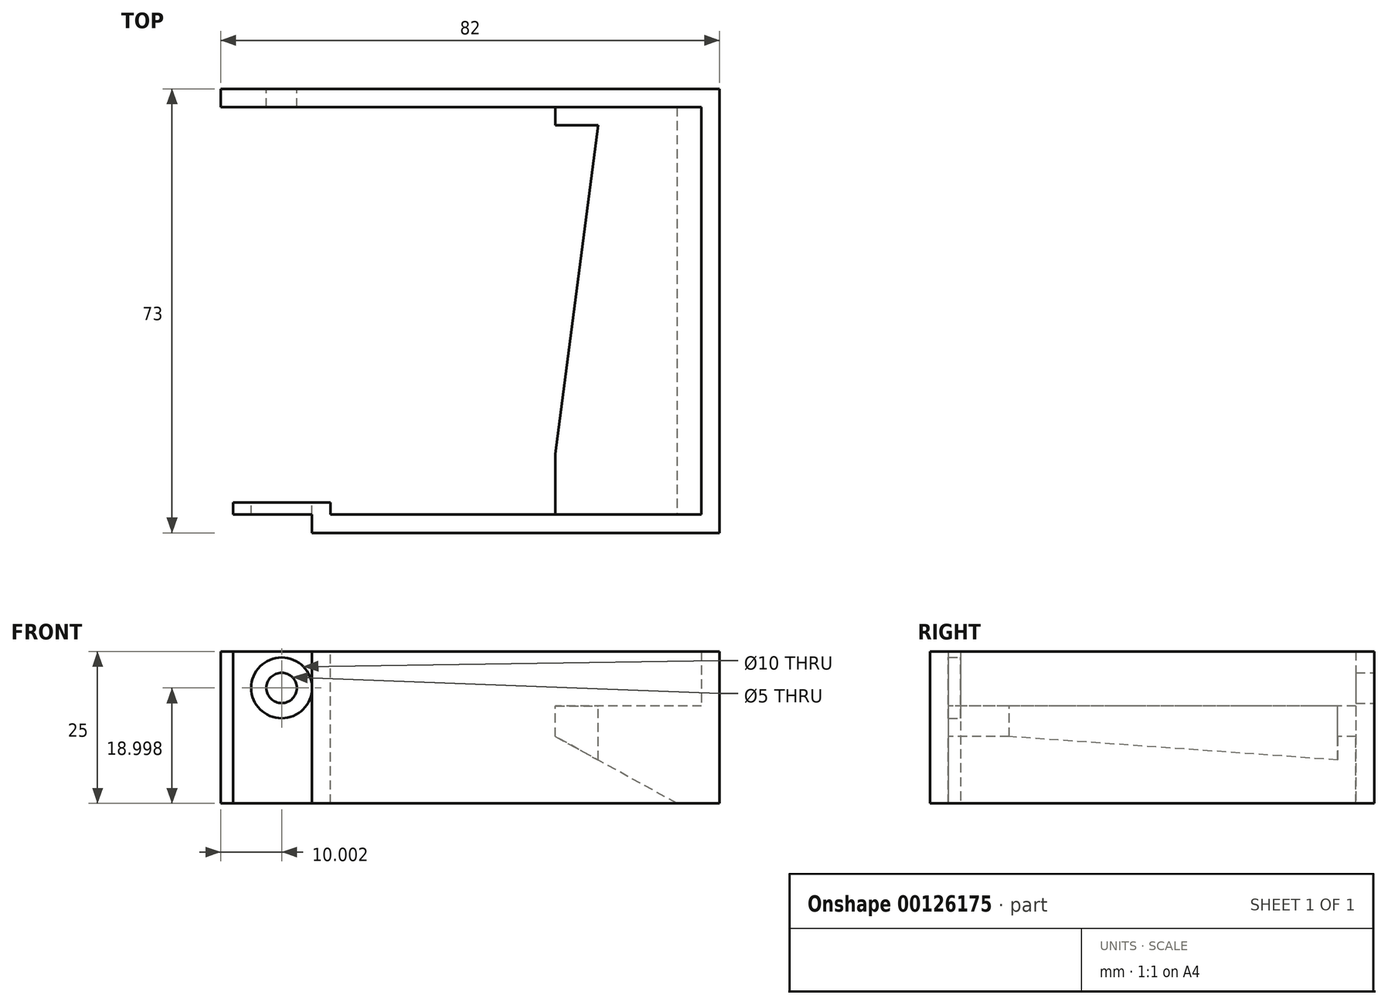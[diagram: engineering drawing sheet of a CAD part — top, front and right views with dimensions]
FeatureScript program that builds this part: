
annotation { "Feature Type Name" : "Feature", "Feature Type Description" : "" }
export const myFeature = defineFeature(function(context is Context, id is Id, definition is map)
    precondition{}
    {
        {
            var Q0;
            Q0=qCreatedBy(makeId("Front.planeOp"),FACE);
            var sketch = newSketch(context, id + "F0", { "sketchPlane" : qUnion([Q0])});
            skLineSegment(sketch, "E0.bottom", {"start": v(-28.48, 9.04) * mm, "end": v(-12.48, 9.04) * mm});
            skLineSegment(sketch, "E0.top", {"start": v(-28.48, -15.96) * mm, "end": v(-12.48, -15.96) * mm});
            skLineSegment(sketch, "E0.left", {"start": v(-28.48, 9.04) * mm, "end": v(-28.48, -15.96) * mm});
            skLineSegment(sketch, "E0.right", {"start": v(-12.48, 9.04) * mm, "end": v(-12.48, -15.96) * mm});
            skLineSegment(sketch, "E1", {"start": v(-20.48, -15.96) * mm, "end": v(-20.48, 3.04) * mm, "construction": true});
            skCircle(sketch, "E2", {"center": v(-20.48, 3.04) * mm, "radius": 5 * mm});
            skLineSegment(sketch, "E3", {"start": v(-28.48, 3.04) * mm, "end": v(-20.48, 3.04) * mm, "construction": true});
            skSolve(sketch);
        }
        {
            var Q0;
            Q0 = qSketchRegion(id + "F0", true);
            extrude(context, id + "F1", {"entities" : qUnion([Q0]), "depth" : 2 * mm});
        }
        {
            var Q0;
            Q0=makeQuery(id+"F1.opExtrude","CAP_FACE",FACE,{"disambiguationData":[OSD([sQuery(id+"F0.wireOp",EDGE,"E0.bottom"),sQuery(id+"F0.wireOp",EDGE,"E0.top"),sQuery(id+"F0.wireOp",EDGE,"E0.left"),sQuery(id+"F0.wireOp",EDGE,"E0.right"),sQuery(id+"F0.wireOp",EDGE,"E2")])],"isStart":false});
            var sketch = newSketch(context, id + "F2", { "sketchPlane" : qUnion([Q0])});
            skLineSegment(sketch, "E4.bottom", {"start": v(-12.48, 9.04) * mm, "end": v(-15.48, 9.04) * mm});
            skLineSegment(sketch, "E4.top", {"start": v(-12.48, -15.96) * mm, "end": v(-15.48, -15.96) * mm});
            skLineSegment(sketch, "E4.left", {"start": v(-12.48, 9.04) * mm, "end": v(-12.48, -15.96) * mm});
            skLineSegment(sketch, "E4.right", {"start": v(-15.48, 9.04) * mm, "end": v(-15.48, -15.96) * mm});
            skSolve(sketch);
        }
        {
            var Q0;
            Q0 = qSketchRegion(id + "F2", true);
            extrude(context, id + "F3", {"entities" : qUnion([Q0]), "operationType" : NewBodyOperationType.ADD, "depth" : 3 * mm});
        }
        {
            var Q0;
            Q0=makeQuery(id+"F3.boolean.opBoolean","MERGE",FACE,{"derivedFrom":[makeQuery(id+"F1.opExtrude","SWEPT_FACE",FACE,{"disambiguationData":[OSD([sQuery(id+"F0.wireOp",EDGE,"E0.right")])]}),makeQuery(id+"F3.opExtrude","SWEPT_FACE",FACE,{"disambiguationData":[OSD([sQuery(id+"F2.wireOp",EDGE,"E4.left")])]})]});
            var sketch = newSketch(context, id + "F4", { "sketchPlane" : qUnion([Q0])});
            skLineSegment(sketch, "E5.bottom", {"start": v(-5, -15.96) * mm, "end": v(-2, -15.96) * mm});
            skLineSegment(sketch, "E5.top", {"start": v(-5, 9.04) * mm, "end": v(-2, 9.04) * mm});
            skLineSegment(sketch, "E5.left", {"start": v(-5, -15.96) * mm, "end": v(-5, 9.04) * mm});
            skLineSegment(sketch, "E5.right", {"start": v(-2, -15.96) * mm, "end": v(-2, 9.04) * mm});
            skSolve(sketch);
        }
        {
            var Q0;
            Q0 = qSketchRegion(id + "F4", true);
            extrude(context, id + "F5", {"entities" : qUnion([Q0]), "operationType" : NewBodyOperationType.ADD, "depth" : 65 * mm});
        }
        {
            var Q0;
            Q0=makeQuery(id+"F5.opExtrude","SWEPT_FACE",FACE,{"disambiguationData":[OSD([sQuery(id+"F4.wireOp",EDGE,"E5.right")])]});
            var sketch = newSketch(context, id + "F6", { "sketchPlane" : qUnion([Q0])});
            skLineSegment(sketch, "E6.bottom", {"start": v(-52.52, 9.04) * mm, "end": v(-49.52, 9.04) * mm});
            skLineSegment(sketch, "E6.top", {"start": v(-52.52, -15.96) * mm, "end": v(-49.52, -15.96) * mm});
            skLineSegment(sketch, "E6.left", {"start": v(-52.52, 9.04) * mm, "end": v(-52.52, -15.96) * mm});
            skLineSegment(sketch, "E6.right", {"start": v(-49.52, 9.04) * mm, "end": v(-49.52, -15.96) * mm});
            skSolve(sketch);
        }
        {
            var Q0;
            Q0 = qSketchRegion(id + "F6", true);
            extrude(context, id + "F7", {"entities" : qUnion([Q0]), "operationType" : NewBodyOperationType.ADD, "depth" : 70 * mm});
        }
        {
            var Q0;
            Q0=makeQuery(id+"F1.opExtrude","CAP_FACE",FACE,{"disambiguationData":[OSD([sQuery(id+"F0.wireOp",EDGE,"E0.bottom"),sQuery(id+"F0.wireOp",EDGE,"E0.top"),sQuery(id+"F0.wireOp",EDGE,"E0.left"),sQuery(id+"F0.wireOp",EDGE,"E0.right"),sQuery(id+"F0.wireOp",EDGE,"E2")])],"isStart":true});
            var sketch = newSketch(context, id + "F8", { "sketchPlane" : qUnion([Q0])});
            skCircle(sketch, "E7", {"center": v(20.48, 3.04) * mm, "radius": 15 * mm, "construction": true});
            skSolve(sketch);
        }
        {
            var Q0;
            Q0=makeQuery(id+"F5.opExtrude","SWEPT_FACE",FACE,{"disambiguationData":[OSD([sQuery(id+"F4.wireOp",EDGE,"E5.right")])]});
            var sketch = newSketch(context, id + "F9", { "sketchPlane" : qUnion([Q0])});
            skLineSegment(sketch, "E8", {"start": v(-49.52, -15.96) * mm, "end": v(-49.52, 0.04) * mm});
            skLineSegment(sketch, "E9", {"start": v(-49.52, 0.04) * mm, "end": v(-24.52, 0.04) * mm});
            skLineSegment(sketch, "E10", {"start": v(20.48, 3.04) * mm, "end": v(-53.47, 3.04) * mm, "construction": true});
            skLineSegment(sketch, "E11", {"start": v(-49.52, -15.96) * mm, "end": v(-44.52, -15.96) * mm});
            skLineSegment(sketch, "E12", {"start": v(-44.52, -15.96) * mm, "end": v(-49.52, -15.96) * mm});
            skLineSegment(sketch, "E13", {"start": v(-24.52, 0.04) * mm, "end": v(-24.52, -4.96) * mm});
            skLineSegment(sketch, "E14", {"start": v(-44.52, -15.96) * mm, "end": v(-24.52, -4.96) * mm});
            skSolve(sketch);
        }
        {
            var Q0;
            Q0 = qSketchRegion(id + "F9", true);
            extrude(context, id + "F10", {"entities" : qUnion([Q0]), "operationType" : NewBodyOperationType.ADD, "depth" : 67 * mm});
        }
        {
            var Q0;
            Q0=makeQuery(id+"F7.opExtrude","SWEPT_FACE",FACE,{"disambiguationData":[OSD([sQuery(id+"F6.wireOp",EDGE,"E6.right")])]});
            var sketch = newSketch(context, id + "F11", { "sketchPlane" : qUnion([Q0])});
            skLineSegment(sketch, "E15.bottom", {"start": v(-68, 9.04) * mm, "end": v(-65, 9.04) * mm});
            skLineSegment(sketch, "E15.top", {"start": v(-68, -15.96) * mm, "end": v(-65, -15.96) * mm});
            skLineSegment(sketch, "E15.left", {"start": v(-68, 9.04) * mm, "end": v(-68, -15.96) * mm});
            skLineSegment(sketch, "E15.right", {"start": v(-65, 9.04) * mm, "end": v(-65, -15.96) * mm});
            skSolve(sketch);
        }
        {
            var Q0;
            Q0 = qSketchRegion(id + "F11", true);
            extrude(context, id + "F12", {"entities" : qUnion([Q0]), "operationType" : NewBodyOperationType.ADD, "depth" : 80 * mm});
        }
        {
            var Q0;
            Q0=makeQuery(id+"F12.boolean.opBoolean","MERGE",FACE,{"derivedFrom":[makeQuery(id+"F7.opExtrude","CAP_FACE",FACE,{"disambiguationData":[OSD([sQuery(id+"F6.wireOp",EDGE,"E6.bottom"),sQuery(id+"F6.wireOp",EDGE,"E6.top"),sQuery(id+"F6.wireOp",EDGE,"E6.left"),sQuery(id+"F6.wireOp",EDGE,"E6.right")])],"isStart":false}),makeQuery(id+"F12.opExtrude","SWEPT_FACE",FACE,{"disambiguationData":[OSD([sQuery(id+"F11.wireOp",EDGE,"E15.left")])]})]});
            var sketch = newSketch(context, id + "F13", { "sketchPlane" : qUnion([Q0])});
            skCircle(sketch, "E16", {"center": v(20.48, 3.04) * mm, "radius": 2.5 * mm});
            skSolve(sketch);
        }
        {
            var Q0;
            Q0 = qSketchRegion(id + "F13", true);
            extrude(context, id + "F14", {"entities" : qUnion([Q0]), "operationType" : NewBodyOperationType.REMOVE, "oppositeDirection" : true, "depth" : 3 * mm});
        }
        {
            var Q0;
            Q0=makeQuery(id+"F10.opExtrude","SWEPT_FACE",FACE,{"disambiguationData":[OSD([sQuery(id+"F9.wireOp",EDGE,"E9")])]});
            var sketch = newSketch(context, id + "F15", { "sketchPlane" : qUnion([Q0])});
            skLineSegment(sketch, "E17", {"start": v(24.52, 65) * mm, "end": v(24.52, 62) * mm, "construction": true});
            skLineSegment(sketch, "E18", {"start": v(24.52, 62) * mm, "end": v(24.52, 8) * mm});
            skLineSegment(sketch, "E19", {"start": v(24.52, 62) * mm, "end": v(31.52, 62) * mm});
            skLineSegment(sketch, "E20", {"start": v(31.52, 62) * mm, "end": v(24.52, 8) * mm});
            skLineSegment(sketch, "E21", {"start": v(31.52, 62) * mm, "end": v(49.52, 62) * mm, "construction": true});
            skSolve(sketch);
        }
        {
            var Q0;
            Q0 = qSketchRegion(id + "F15", true);
            extrude(context, id + "F16", {"entities" : qUnion([Q0]), "operationType" : NewBodyOperationType.REMOVE, "endBound" : BoundingType.THROUGH_ALL, "oppositeDirection" : true, "depth" : 25 * mm});
        }
        {
            var Q0;
            Q0=makeQuery(id+"F10.opExtrude","SWEPT_FACE",FACE,{"disambiguationData":[OSD([sQuery(id+"F9.wireOp",EDGE,"E9")])]});
            var sketch = newSketch(context, id + "F17", { "sketchPlane" : qUnion([Q0])});
            skLineSegment(sketch, "E22.bottom", {"start": v(49.52, 65) * mm, "end": v(48.52, 65) * mm});
            skLineSegment(sketch, "E22.top", {"start": v(49.52, -2) * mm, "end": v(48.52, -2) * mm});
            skLineSegment(sketch, "E22.left", {"start": v(49.52, 65) * mm, "end": v(49.52, -2) * mm});
            skLineSegment(sketch, "E22.right", {"start": v(48.52, 65) * mm, "end": v(48.52, -2) * mm});
            skSolve(sketch);
        }
        {
            var Q0;
            Q0 = qSketchRegion(id + "F17", true);
            var Q1;
            {var subQ1=sQuery(id+"F0.wireOp",EDGE,"E0.left");var subQ3=sQuery(id+"F2.wireOp",EDGE,"E4.bottom");var subQ7=sQuery(id+"F0.wireOp",EDGE,"E0.bottom");var subQ10=sQuery(id+"F4.wireOp",EDGE,"E5.top");var subQ13=sQuery(id+"F6.wireOp",EDGE,"E6.bottom");Q1=makeQuery(id+"F14.boolean.opBoolean","SPLIT",FACE,{"disambiguationData":[TD([makeQuery(id+"F1.opExtrude","SWEPT_FACE",FACE,{"disambiguationData":[OSD([subQ1])]})])],"derivedFrom":makeQuery(id+"F12.boolean.opBoolean","MERGE",FACE,{"derivedFrom":[makeQuery(id+"F7.boolean.opBoolean","MERGE",FACE,{"derivedFrom":[makeQuery(id+"F5.boolean.opBoolean","MERGE",FACE,{"derivedFrom":[makeQuery(id+"F3.boolean.opBoolean","MERGE",FACE,{"derivedFrom":[makeQuery(id+"F1.opExtrude","SWEPT_FACE",FACE,{"disambiguationData":[OSD([subQ7])]}),makeQuery(id+"F3.opExtrude","SWEPT_FACE",FACE,{"disambiguationData":[OSD([subQ3])]})]}),makeQuery(id+"F5.opExtrude","SWEPT_FACE",FACE,{"disambiguationData":[OSD([subQ10])]})]}),makeQuery(id+"F7.opExtrude","SWEPT_FACE",FACE,{"disambiguationData":[OSD([subQ13])]})]}),makeQuery(id+"F12.opExtrude","SWEPT_FACE",FACE,{"disambiguationData":[OSD([sQuery(id+"F11.wireOp",EDGE,"E15.bottom")])]})]})});}
            extrude(context, id + "F18", {"entities" : qUnion([Q0]), "operationType" : NewBodyOperationType.ADD, "endBound" : BoundingType.UP_TO_SURFACE, "endBoundEntityFace" : qUnion([Q1]), "depth" : 25 * mm});
        }
        {
            var Q0;
            {var subQ1=sQuery(id+"F0.wireOp",EDGE,"E0.left");var subQ3=sQuery(id+"F2.wireOp",EDGE,"E4.bottom");var subQ7=sQuery(id+"F0.wireOp",EDGE,"E0.bottom");var subQ10=sQuery(id+"F4.wireOp",EDGE,"E5.top");var subQ13=sQuery(id+"F6.wireOp",EDGE,"E6.bottom");Q0=makeQuery(id+"F18.boolean.opBoolean","MERGE",FACE,{"derivedFrom":[makeQuery(id+"F14.boolean.opBoolean","SPLIT",FACE,{"disambiguationData":[TD([makeQuery(id+"F1.opExtrude","SWEPT_FACE",FACE,{"disambiguationData":[OSD([subQ1])]})])],"derivedFrom":makeQuery(id+"F12.boolean.opBoolean","MERGE",FACE,{"derivedFrom":[makeQuery(id+"F7.boolean.opBoolean","MERGE",FACE,{"derivedFrom":[makeQuery(id+"F5.boolean.opBoolean","MERGE",FACE,{"derivedFrom":[makeQuery(id+"F3.boolean.opBoolean","MERGE",FACE,{"derivedFrom":[makeQuery(id+"F1.opExtrude","SWEPT_FACE",FACE,{"disambiguationData":[OSD([subQ7])]}),makeQuery(id+"F3.opExtrude","SWEPT_FACE",FACE,{"disambiguationData":[OSD([subQ3])]})]}),makeQuery(id+"F5.opExtrude","SWEPT_FACE",FACE,{"disambiguationData":[OSD([subQ10])]})]}),makeQuery(id+"F7.opExtrude","SWEPT_FACE",FACE,{"disambiguationData":[OSD([subQ13])]})]}),makeQuery(id+"F12.opExtrude","SWEPT_FACE",FACE,{"disambiguationData":[OSD([sQuery(id+"F11.wireOp",EDGE,"E15.bottom")])]})]})}),makeQuery(id+"F18.opExtrude","CAP_FACE",FACE,{"disambiguationData":[OSD([sQuery(id+"F17.wireOp",EDGE,"E22.bottom"),sQuery(id+"F17.wireOp",EDGE,"E22.top"),sQuery(id+"F17.wireOp",EDGE,"E22.left"),sQuery(id+"F17.wireOp",EDGE,"E22.right")])],"isStart":false})]});}
            var sketch = newSketch(context, id + "F19", { "sketchPlane" : qUnion([Q0])});
            skLineSegment(sketch, "E23.bottom", {"start": v(52.52, 68) * mm, "end": v(51.52, 68) * mm});
            skLineSegment(sketch, "E23.top", {"start": v(52.52, -5) * mm, "end": v(51.52, -5) * mm});
            skLineSegment(sketch, "E23.left", {"start": v(52.52, 68) * mm, "end": v(52.52, -5) * mm});
            skLineSegment(sketch, "E23.right", {"start": v(51.52, 68) * mm, "end": v(51.52, -5) * mm});
            skSolve(sketch);
        }
        {
            var Q0;
            Q0 = qSketchRegion(id + "F19", true);
            extrude(context, id + "F20", {"entities" : qUnion([Q0]), "operationType" : NewBodyOperationType.REMOVE, "endBound" : BoundingType.THROUGH_ALL, "oppositeDirection" : true, "depth" : 25 * mm});
        }
    });
